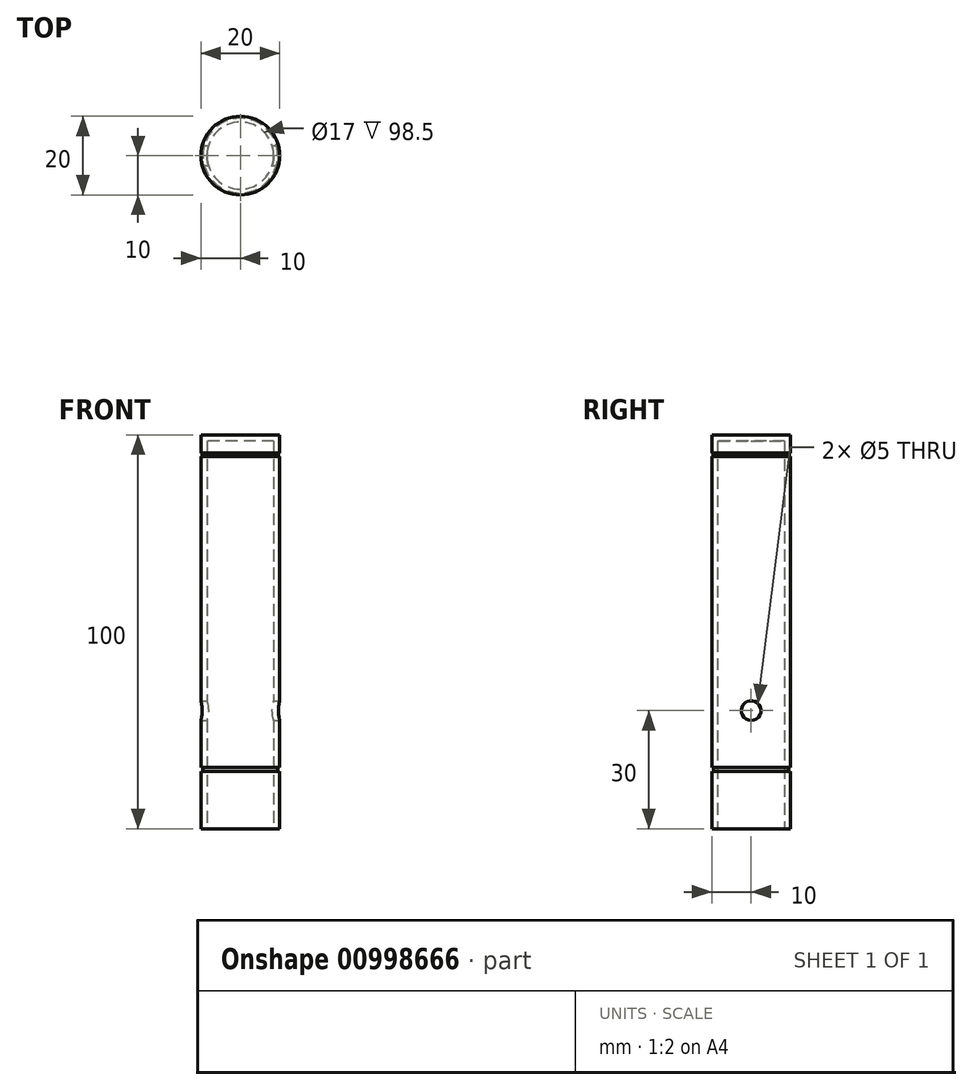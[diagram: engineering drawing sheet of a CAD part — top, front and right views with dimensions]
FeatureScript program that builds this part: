
annotation { "Feature Type Name" : "Feature", "Feature Type Description" : "" }
export const myFeature = defineFeature(function(context is Context, id is Id, definition is map)
    precondition{}
    {
        {
            var Q0;
            Q0=qCreatedBy(makeId("Top.planeOp"),FACE);
            var sketch = newSketch(context, id + "F0", { "sketchPlane" : qUnion([Q0])});
            skCircle(sketch, "E0", {"center": v(0, 0) * mm, "radius": 10 * mm});
            skCircle(sketch, "E1.0", {"center": v(0, 0) * mm, "radius": 8.5 * mm});
            skSolve(sketch);
        }
        {
            var Q0;
            Q0=makeQuery(id+"F0.imprint","IMPRINT",FACE,{"disambiguationData":[TD([[makeQuery(id+"F0.imprint","IMPRINT",EDGE,{"derivedFrom":sQuery(id+"F0.wireOp",EDGE,"E0")}),1.0]])]});
            extrude(context, id + "F1", {"entities" : qUnion([Q0]), "endBound" : BoundingType.SYMMETRIC, "depth" : 100 * mm, "offsetDistance" : 25 * mm});
        }
        {
            var Q0;
            Q0=makeQuery(id+"F1.opExtrude","CAP_FACE",FACE,{"disambiguationData":[OSD([sQuery(id+"F0.wireOp",EDGE,"E0"),sQuery(id+"F0.wireOp",EDGE,"E1.0")])],"isStart":false});
            var sketch = newSketch(context, id + "F2", { "sketchPlane" : qUnion([Q0])});
            skCircle(sketch, "E2", {"center": v(0, 0) * mm, "radius": 8.5 * mm});
            skSolve(sketch);
        }
        {
            var Q0;
            Q0=qSketchRegion(id+"F2",true);
            extrude(context, id + "F3", {"entities" : qUnion([Q0]), "operationType" : NewBodyOperationType.ADD, "oppositeDirection" : true, "depth" : 1.5 * mm, "offsetDistance" : 25 * mm});
        }
        {
            var Q0;
            Q0=qCreatedBy(makeId("Right.planeOp"),FACE);
            var sketch = newSketch(context, id + "F4", { "sketchPlane" : qUnion([Q0])});
            skCircle(sketch, "E3", {"center": v(0, -20) * mm, "radius": 2.5 * mm});
            skSolve(sketch);
        }
        {
            var Q0;
            Q0=qSketchRegion(id+"F4",true);
            extrude(context, id + "F5", {"entities" : qUnion([Q0]), "operationType" : NewBodyOperationType.REMOVE, "endBound" : BoundingType.SYMMETRIC, "oppositeDirection" : true, "depth" : 25 * mm, "offsetDistance" : 25 * mm});
        }
        {
            var Q0;
            Q0=makeQuery(id+"F3.boolean.opBoolean","MERGE",FACE,{"derivedFrom":[makeQuery(id+"F1.opExtrude","CAP_FACE",FACE,{"disambiguationData":[OSD([sQuery(id+"F0.wireOp",EDGE,"E0"),sQuery(id+"F0.wireOp",EDGE,"E1.0")])],"isStart":false}),makeQuery(id+"F3.opExtrude","CAP_FACE",FACE,{"disambiguationData":[OSD([sQuery(id+"F2.wireOp",EDGE,"E2")])],"isStart":true})]});
            cPlane(context, id + "F6", {"entities" : qUnion([Q0]), "cplaneType" : CPlaneType.OFFSET, "offset" : 5 * mm, "oppositeDirection" : true, "width" : 150 * mm, "height" : 150 * mm});
        }
        {
            var Q0;
            Q0=qCreatedBy(id+"F6.planeOp",FACE);
            var sketch = newSketch(context, id + "F7", { "sketchPlane" : qUnion([Q0])});
            skCircle(sketch, "E4", {"center": v(0, 0) * mm, "radius": 10 * mm});
            skCircle(sketch, "E5.0", {"center": v(0, 0) * mm, "radius": 9.75 * mm});
            skSolve(sketch);
        }
        {
            var Q0;
            Q0=qSketchRegion(id+"F7",true);
            extrude(context, id + "F8", {"entities" : qUnion([Q0]), "operationType" : NewBodyOperationType.REMOVE, "endBound" : BoundingType.SYMMETRIC, "oppositeDirection" : true, "depth" : 1 * mm, "offsetDistance" : 25 * mm});
        }
        {
            var Q0;
            Q0=makeQuery(id+"FIudg7CWSzi0N1h_1.1.F3.boolean.opBoolean","MERGE",FACE,{"derivedFrom":[makeQuery(id+"F1.opExtrude","CAP_FACE",FACE,{"disambiguationData":[OSD([sQuery(id+"F0.wireOp",EDGE,"E0"),sQuery(id+"F0.wireOp",EDGE,"E1.0")])],"isStart":true}),makeQuery(id+"FIudg7CWSzi0N1h_1.1.F3.opExtrude","CAP_FACE",FACE,{"disambiguationData":[OSD([sQuery(id+"F2.wireOp",EDGE,"E2")])],"isStart":true})]});
            cPlane(context, id + "F9", {"entities" : qUnion([Q0]), "cplaneType" : CPlaneType.OFFSET, "offset" : 15 * mm, "oppositeDirection" : true, "width" : 150 * mm, "height" : 150 * mm});
        }
        {
            var Q0;
            Q0=qCreatedBy(id+"F9.planeOp",FACE);
            var sketch = newSketch(context, id + "F10", { "sketchPlane" : qUnion([Q0])});
            skCircle(sketch, "E6", {"center": v(0, 0) * mm, "radius": 10 * mm});
            skCircle(sketch, "E7.0", {"center": v(0, 0) * mm, "radius": 9.5 * mm});
            skSolve(sketch);
        }
        {
            var Q0;
            Q0=qSketchRegion(id+"F10",true);
            extrude(context, id + "F11", {"entities" : qUnion([Q0]), "operationType" : NewBodyOperationType.REMOVE, "endBound" : BoundingType.SYMMETRIC, "oppositeDirection" : true, "depth" : 1 * mm, "offsetDistance" : 25 * mm});
        }
    });
